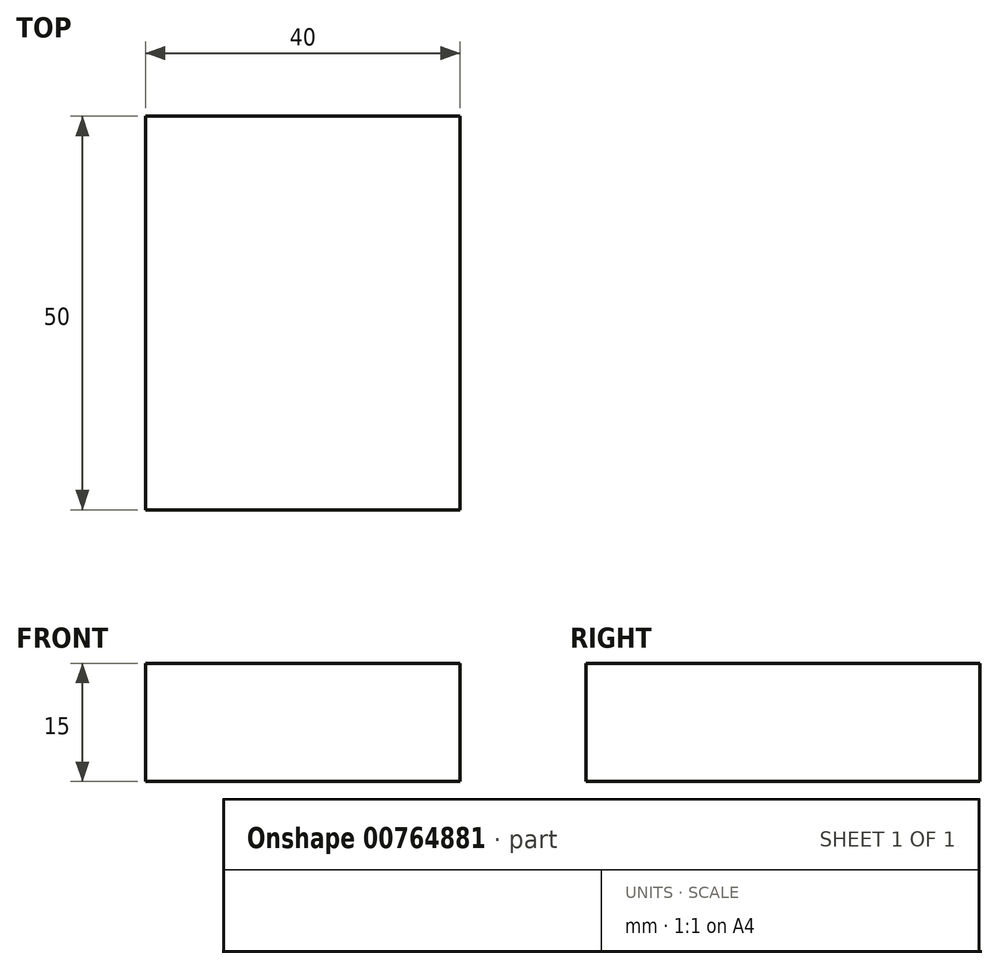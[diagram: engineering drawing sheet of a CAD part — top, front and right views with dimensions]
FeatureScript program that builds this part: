
annotation { "Feature Type Name" : "Feature", "Feature Type Description" : "" }
export const myFeature = defineFeature(function(context is Context, id is Id, definition is map)
    precondition{}
    {
        {
            var Q0;
            Q0=qCreatedBy(makeId("Top.planeOp"),FACE);
            var sketch = newSketch(context, id + "F0", { "sketchPlane" : qUnion([Q0])});
            skLineSegment(sketch, "E0.bottom", {"start": v(0, 0) * mm, "end": v(40, 0) * mm});
            skLineSegment(sketch, "E0.top", {"start": v(0, 50) * mm, "end": v(40, 50) * mm});
            skLineSegment(sketch, "E0.left", {"start": v(0, 0) * mm, "end": v(0, 50) * mm});
            skLineSegment(sketch, "E0.right", {"start": v(40, 0) * mm, "end": v(40, 50) * mm});
            skSolve(sketch);
        }
        {
            var Q0;
            Q0=makeQuery(id+"F0.imprint","IMPRINT",FACE,{"disambiguationData":[TD([[makeQuery(id+"F0.imprint","IMPRINT",EDGE,{"derivedFrom":sQuery(id+"F0.wireOp",EDGE,"E0.bottom")}),1.0]])]});
            extrude(context, id + "F1", {"entities" : qUnion([Q0]), "depth" : 15 * mm, "offsetDistance" : 25 * mm});
        }
    });
